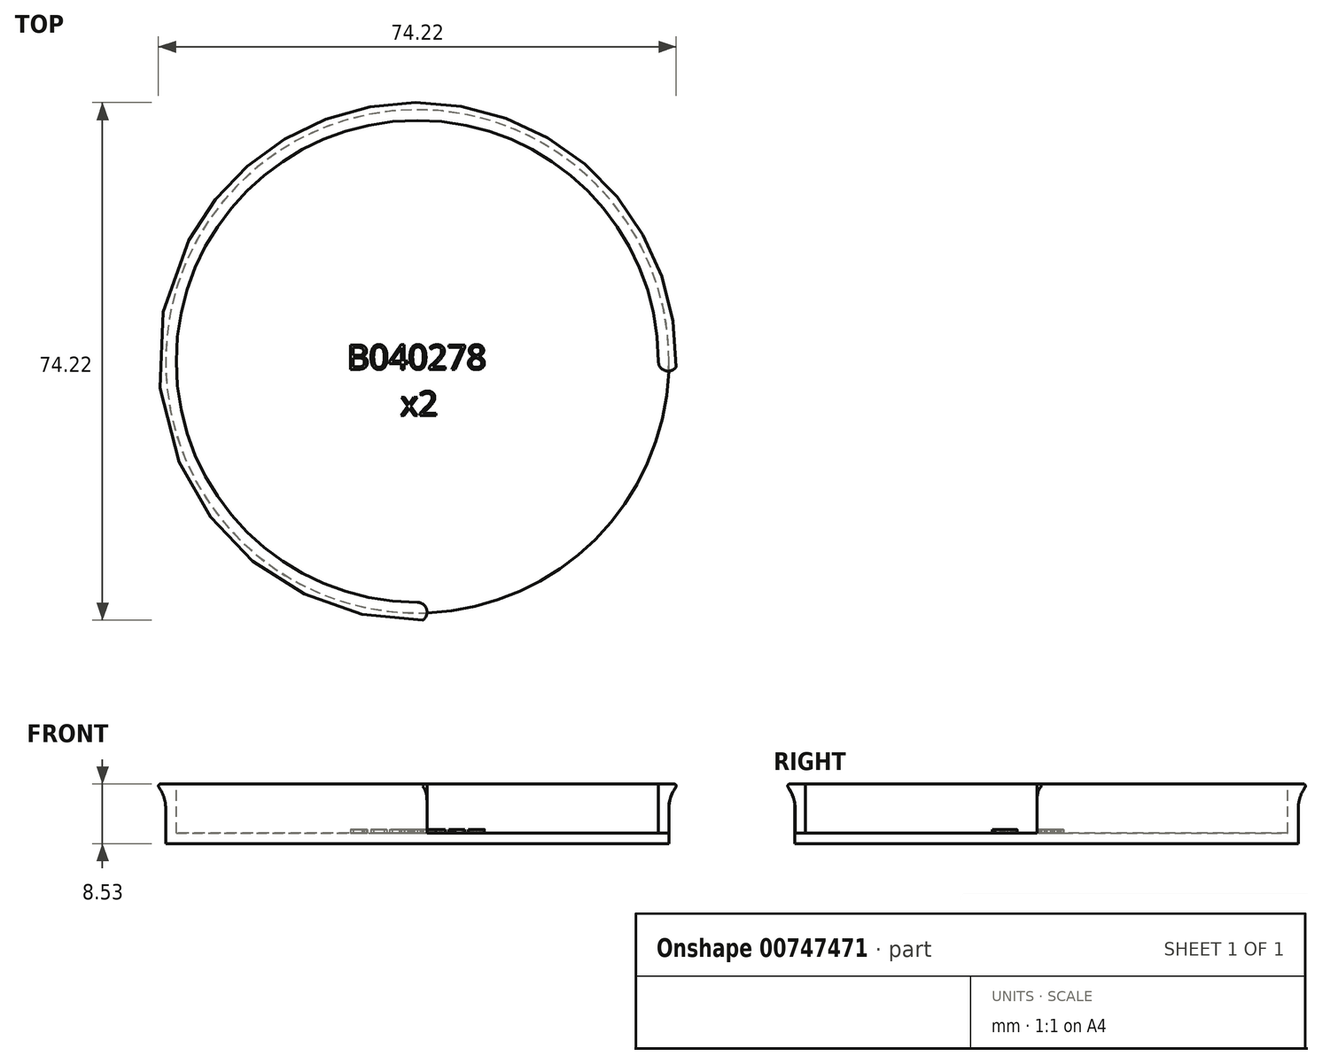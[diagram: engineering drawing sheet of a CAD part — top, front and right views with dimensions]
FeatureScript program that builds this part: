
annotation { "Feature Type Name" : "Feature", "Feature Type Description" : "" }
export const myFeature = defineFeature(function(context is Context, id is Id, definition is map)
    precondition{}
    {
        {
            var Q0;
            Q0=qCreatedBy(makeId("Right.planeOp"),FACE);
            var sketch = newSketch(context, id + "F0", { "sketchPlane" : qUnion([Q0])});
            skLineSegment(sketch, "E0", {"start": v(21.43, 8.53) * mm, "end": v(21.43, 0) * mm});
            skLineSegment(sketch, "E1", {"start": v(21.43, 8.53) * mm, "end": v(-15.93, 8.53) * mm});
            skLineSegment(sketch, "E2", {"start": v(21.43, 0) * mm, "end": v(-14.66, 0) * mm});
            skLineSegment(sketch, "E3", {"start": v(-14.66, 0) * mm, "end": v(-14.66, 6.5) * mm});
            skLineSegment(sketch, "E4", {"start": v(-14.66, 6.5) * mm, "end": v(-14.66, 8.53) * mm});
            skLineSegment(sketch, "E5", {"start": v(-15.93, 8.53) * mm, "end": v(-14.66, 6.5) * mm});
            skSolve(sketch);
        }
        {
            var Q0;
            Q0=qSketchRegion(id+"F0",true);
            var Q1;
            Q1=sQuery(id+"F0.wireOp",EDGE,"E0");
            revolve(context, id + "F1", {"entities" : qUnion([Q0]), "axis" : qUnion([Q1]), "revolveType" : RevolveType.FULL});
        }
        {
            var Q0;
            Q0=makeQuery(id+"F1.opRevolve","SWEPT_FACE",FACE,{"disambiguationData":[OSD([sQuery(id+"F0.wireOp",EDGE,"E1")])]});
            var sketch = newSketch(context, id + "F2", { "sketchPlane" : qUnion([Q0])});
            skArc(sketch, "E6", {"start": v(0, -15.93) * mm, "mid": v(1.4, -14.53) * mm, "end": v(0, -13.13) * mm});
            skCircle(sketch, "E7", {"center": v(0, 21.43) * mm, "radius": 34.56 * mm});
            skLineSegment(sketch, "E8", {"start": v(0, 21.43) * mm, "end": v(37.35, 21.43) * mm});
            skArc(sketch, "E9", {"start": v(34.56, 21.43) * mm, "mid": v(35.95, 20.03) * mm, "end": v(37.35, 21.43) * mm});
            skSolve(sketch);
        }
        {
            var Q0;
            {var subQ0=sQuery(id+"F2.wireOp",EDGE,"E6");Q0=makeQuery(id+"F2.imprint","IMPRINT",FACE,{"disambiguationData":[TD([[makeQuery(id+"F2.imprint","IMPRINT",EDGE,{"derivedFrom":subQ0}),-1.0]])]});}
            var Q1;
            {var subQ0=sQuery(id+"F2.wireOp",EDGE,"E7");var subQ1=makeQuery(id+"F2.imprint","INTERSECT",VERTEX,{"derivedFrom":[sQuery(id+"F2.wireOp",EDGE,"E6"),subQ0]});Q1=makeQuery(id+"F2.imprint","IMPRINT",FACE,{"disambiguationData":[TD([[makeQuery(id+"F2.imprint","IMPRINT",EDGE,{"disambiguationData":[TD([[subQ1,1.0]])],"derivedFrom":subQ0}),1.0]])]});}
            extrude(context, id + "F3", {"entities" : qUnion([Q0, Q1]), "operationType" : NewBodyOperationType.REMOVE, "oppositeDirection" : true, "depth" : 7 * mm});
        }
        {
            var Q0;
            Q0=makeQuery(id+"F1.opRevolve","SWEPT_EDGE",EDGE,{"disambiguationData":[OSD([sQuery(id+"F0.wireOp",EDGE,"E1"),sQuery(id+"F0.wireOp",EDGE,"E5")])]});
            var Q1;
            Q1=makeQuery(id+"F3.boolean.opBoolean","COPY",EDGE,{"derivedFrom":makeQuery(id+"F3.opExtrude","CAP_EDGE",EDGE,{"disambiguationData":[OSD([sQuery(id+"F2.wireOp",EDGE,"Hj940JX0-86ln-aeAX-7QBq-tXhmjeFzDDCG")])],"isStart":true})});
            fillet(context, id + "F4", {"entities" : qUnion([Q0, Q1]), "radius" : 0.3 * mm, "tangentPropagation" : true, "allowEdgeOverflow" : false});
        }
        {
            var Q0;
            Q0=makeQuery(id+"F1.opRevolve","SWEPT_EDGE",EDGE,{"disambiguationData":[OSD([sQuery(id+"F0.wireOp",EDGE,"E3"),sQuery(id+"F0.wireOp",EDGE,"E4"),sQuery(id+"F0.wireOp",EDGE,"E5")])]});
            fillet(context, id + "F5", {"entities" : qUnion([Q0]), "radius" : 5 * mm, "tangentPropagation" : true, "allowEdgeOverflow" : false});
        }
        {
            var Q0;
            Q0=makeQuery(id+"F3.boolean.opBoolean","COPY",FACE,{"derivedFrom":makeQuery(id+"F3.opExtrude","CAP_FACE",FACE,{"disambiguationData":[OSD([sQuery(id+"F0.wireOp",EDGE,"E1"),sQuery(id+"F0.wireOp",EDGE,"E5"),sQuery(id+"F2.wireOp",EDGE,"Hj940JX0-86ln-aeAX-7QBq-tXhmjeFzDDCG"),sQuery(id+"F2.wireOp",EDGE,"E6"),sQuery(id+"F2.wireOp",EDGE,"103zpbTG-KLVD-Bw5I-Qeg4-O77QYgVRE0Vj")])],"isStart":false})});
            var sketch = newSketch(context, id + "F6", { "sketchPlane" : qUnion([Q0])});
            skText(sketch, "E10", { "text": "B040278\n      x2", "fontName": "OpenSans-Regular.ttf"});
            const initialGuessF6  = {"E10": [-0.01006, 0.02029, 1, 0, 0.00352]};
            skSetInitialGuess(sketch, initialGuessF6);
            skSolve(sketch);
        }
        {
            var Q0;
            Q0=qSketchRegion(id+"F6",true);
            extrude(context, id + "F7", {"entities" : qUnion([Q0]), "operationType" : NewBodyOperationType.ADD, "depth" : 0.5 * mm, "offsetDistance" : 25 * mm});
        }
    });
